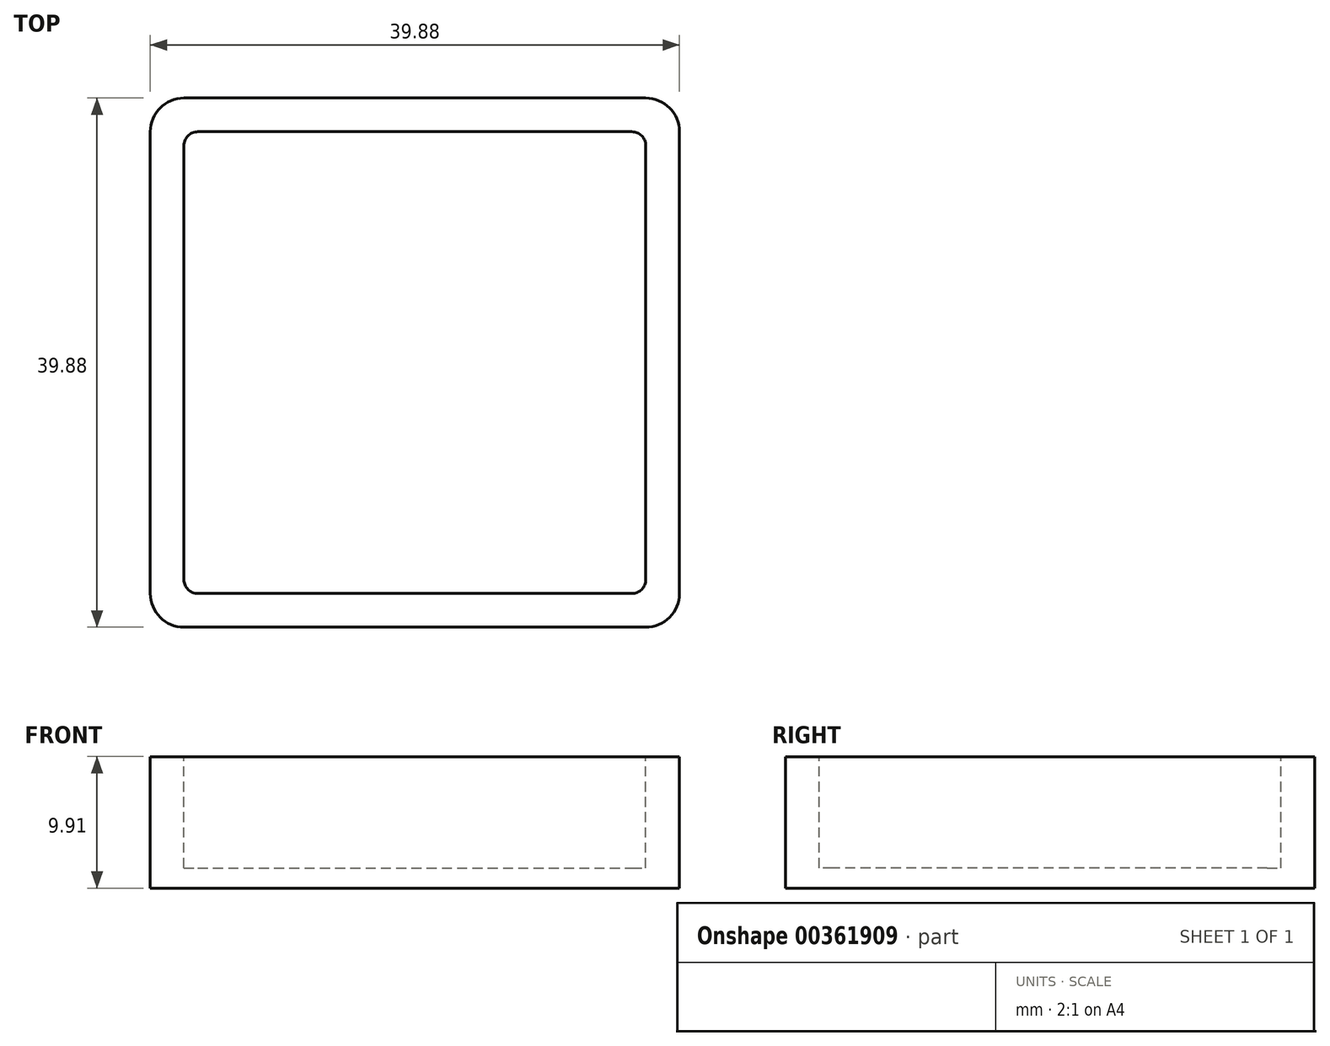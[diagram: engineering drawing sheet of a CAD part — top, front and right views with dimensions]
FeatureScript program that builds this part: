
annotation { "Feature Type Name" : "Feature", "Feature Type Description" : "" }
export const myFeature = defineFeature(function(context is Context, id is Id, definition is map)
    precondition{}
    {
        {
            var Q0;
            Q0=qCreatedBy(makeId("Top.planeOp"),FACE);
            var sketch = newSketch(context, id + "F0", { "sketchPlane" : qUnion([Q0])});
            skLineSegment(sketch, "E0.bottom", {"start": v(-26.4, 16.18) * mm, "end": v(13.47, 16.18) * mm});
            skLineSegment(sketch, "E0.top", {"start": v(-26.4, -23.7) * mm, "end": v(13.47, -23.7) * mm});
            skLineSegment(sketch, "E0.left", {"start": v(-26.4, 16.18) * mm, "end": v(-26.4, -23.7) * mm});
            skLineSegment(sketch, "E0.right", {"start": v(13.47, 16.18) * mm, "end": v(13.47, -23.7) * mm});
            skSolve(sketch);
        }
        {
            var Q0;
            Q0 = qSketchRegion(id + "F0", true);
            extrude(context, id + "F1", {"entities" : qUnion([Q0]), "depth" : 9.9 * mm});
        }
        {
            var Q0;
            Q0=makeQuery(id+"F1.opExtrude","SWEPT_EDGE",EDGE,{"disambiguationData":[OSD([sQuery(id+"F0.wireOp",EDGE,"E0.top"),sQuery(id+"F0.wireOp",EDGE,"E0.right")])]});
            var Q1;
            Q1=makeQuery(id+"F1.opExtrude","SWEPT_EDGE",EDGE,{"disambiguationData":[OSD([sQuery(id+"F0.wireOp",EDGE,"E0.top"),sQuery(id+"F0.wireOp",EDGE,"E0.left")])]});
            var Q2;
            Q2=makeQuery(id+"F1.opExtrude","SWEPT_EDGE",EDGE,{"disambiguationData":[OSD([sQuery(id+"F0.wireOp",EDGE,"E0.bottom"),sQuery(id+"F0.wireOp",EDGE,"E0.left")])]});
            var Q3;
            Q3=makeQuery(id+"F1.opExtrude","SWEPT_EDGE",EDGE,{"disambiguationData":[OSD([sQuery(id+"F0.wireOp",EDGE,"E0.bottom"),sQuery(id+"F0.wireOp",EDGE,"E0.right")])]});
            fillet(context, id + "F2", {"entities" : qUnion([Q0, Q1, Q2, Q3]), "radius" : 2.54 * mm, "tangentPropagation" : true, "allowEdgeOverflow" : false});
        }
        {
            var Q0;
            Q0=makeQuery(id+"F1.opExtrude","CAP_FACE",FACE,{"disambiguationData":[OSD([sQuery(id+"F0.wireOp",EDGE,"E0.bottom"),sQuery(id+"F0.wireOp",EDGE,"E0.top"),sQuery(id+"F0.wireOp",EDGE,"E0.left"),sQuery(id+"F0.wireOp",EDGE,"E0.right")])],"isStart":false});
            var sketch = newSketch(context, id + "F3", { "sketchPlane" : qUnion([Q0])});
            skLineSegment(sketch, "E1.bottom", {"start": v(-23.87, 13.64) * mm, "end": v(10.93, 13.64) * mm});
            skLineSegment(sketch, "E1.top", {"start": v(-23.87, -21.16) * mm, "end": v(10.93, -21.16) * mm});
            skLineSegment(sketch, "E1.left", {"start": v(-23.87, 13.64) * mm, "end": v(-23.87, -21.16) * mm});
            skLineSegment(sketch, "E1.right", {"start": v(10.93, 13.64) * mm, "end": v(10.93, -21.16) * mm});
            skSolve(sketch);
        }
        {
            var Q0;
            Q0 = qSketchRegion(id + "F3", true);
            extrude(context, id + "F4", {"entities" : qUnion([Q0]), "operationType" : NewBodyOperationType.REMOVE, "oppositeDirection" : true, "depth" : 8.38 * mm});
        }
        {
            var Q0;
            Q0=makeQuery(id+"F4.boolean.opBoolean","COPY",EDGE,{"derivedFrom":makeQuery(id+"F4.opExtrude","SWEPT_EDGE",EDGE,{"disambiguationData":[OSD([sQuery(id+"F3.wireOp",EDGE,"E1.bottom"),sQuery(id+"F3.wireOp",EDGE,"E1.left")])]})});
            var Q1;
            Q1=makeQuery(id+"F4.boolean.opBoolean","COPY",EDGE,{"derivedFrom":makeQuery(id+"F4.opExtrude","SWEPT_EDGE",EDGE,{"disambiguationData":[OSD([sQuery(id+"F3.wireOp",EDGE,"E1.bottom"),sQuery(id+"F3.wireOp",EDGE,"E1.right")])]})});
            var Q2;
            Q2=makeQuery(id+"F4.boolean.opBoolean","COPY",EDGE,{"derivedFrom":makeQuery(id+"F4.opExtrude","SWEPT_EDGE",EDGE,{"disambiguationData":[OSD([sQuery(id+"F3.wireOp",EDGE,"E1.top"),sQuery(id+"F3.wireOp",EDGE,"E1.right")])]})});
            var Q3;
            Q3=makeQuery(id+"F4.boolean.opBoolean","COPY",EDGE,{"derivedFrom":makeQuery(id+"F4.opExtrude","SWEPT_EDGE",EDGE,{"disambiguationData":[OSD([sQuery(id+"F3.wireOp",EDGE,"E1.top"),sQuery(id+"F3.wireOp",EDGE,"E1.left")])]})});
            fillet(context, id + "F5", {"entities" : qUnion([Q0, Q1, Q2, Q3]), "radius" : 1.04 * mm, "tangentPropagation" : true, "allowEdgeOverflow" : false});
        }
    });
